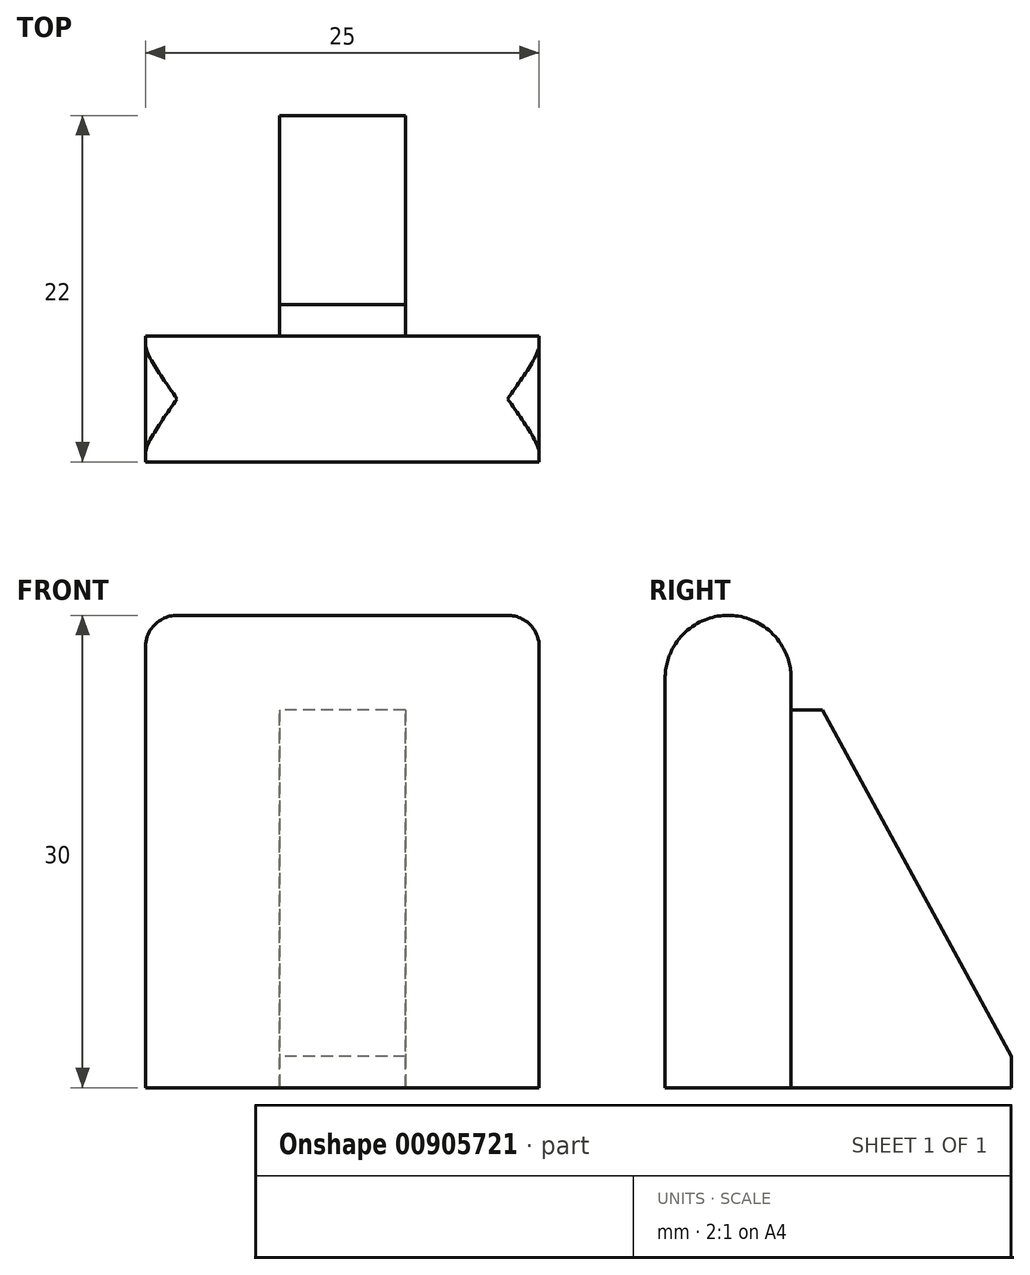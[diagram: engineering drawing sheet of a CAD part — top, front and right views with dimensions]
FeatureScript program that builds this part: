
annotation { "Feature Type Name" : "Feature", "Feature Type Description" : "" }
export const myFeature = defineFeature(function(context is Context, id is Id, definition is map)
    precondition{}
    {
        {
            var Q0;
            Q0=qCreatedBy(makeId("Right.planeOp"),FACE);
            var sketch = newSketch(context, id + "F0", { "sketchPlane" : qUnion([Q0])});
            skLineSegment(sketch, "E0.bottom", {"start": v(0, 0) * mm, "end": v(8, 0) * mm});
            skLineSegment(sketch, "E0.top", {"start": v(0, 26) * mm, "end": v(8, 26) * mm});
            skLineSegment(sketch, "E0.left", {"start": v(0, 0) * mm, "end": v(0, 26) * mm});
            skLineSegment(sketch, "E0.right", {"start": v(8, 0) * mm, "end": v(8, 26) * mm});
            skArc(sketch, "E1", {"start": v(0, 26) * mm, "mid": v(4, 30) * mm, "end": v(8, 26) * mm});
            skSolve(sketch);
        }
        {
            var Q0;
            Q0=makeQuery(id+"F0.imprint","IMPRINT",FACE,{"disambiguationData":[TD([[makeQuery(id+"F0.imprint","IMPRINT",EDGE,{"derivedFrom":sQuery(id+"F0.wireOp",EDGE,"E0.bottom")}),1.0]])]});
            var Q1;
            Q1=makeQuery(id+"F0.imprint","IMPRINT",FACE,{"disambiguationData":[TD([[makeQuery(id+"F0.imprint","IMPRINT",EDGE,{"derivedFrom":sQuery(id+"F0.wireOp",EDGE,"E0.top")}),1.0]])]});
            extrude(context, id + "F1", {"entities" : qUnion([Q0, Q1]), "endBound" : BoundingType.SYMMETRIC, "depth" : 25 * mm, "offsetDistance" : 25 * mm});
        }
        {
            var Q0;
            Q0=qCreatedBy(makeId("Right.planeOp"),FACE);
            var sketch = newSketch(context, id + "F2", { "sketchPlane" : qUnion([Q0])});
            skLineSegment(sketch, "E2.0.0", {"start": v(8, 0) * mm, "end": v(8, 26) * mm});
            skLineSegment(sketch, "E2.0.2", {"start": v(8, 26) * mm, "end": v(8, 0) * mm});
            skLineSegment(sketch, "E3", {"start": v(8, 24) * mm, "end": v(10, 24) * mm});
            skLineSegment(sketch, "E4", {"start": v(10, 24) * mm, "end": v(22, 2) * mm});
            skLineSegment(sketch, "E5", {"start": v(22, 2) * mm, "end": v(22, 0) * mm});
            skLineSegment(sketch, "E6", {"start": v(22, 0) * mm, "end": v(8, 0) * mm});
            skLineSegment(sketch, "E7.0.0", {"start": v(0, 0) * mm, "end": v(8, 0) * mm});
            skLineSegment(sketch, "E7.0.2", {"start": v(8, 0) * mm, "end": v(0, 0) * mm});
            skSolve(sketch);
        }
        {
            var Q0;
            Q0 = qSketchRegion(id + "F2", true);
            extrude(context, id + "F3", {"entities" : qUnion([Q0]), "operationType" : NewBodyOperationType.ADD, "endBound" : BoundingType.SYMMETRIC, "depth" : 8 * mm, "offsetDistance" : 25 * mm});
        }
        {
            var Q0;
            Q0=qCreatedBy(makeId("Front.planeOp"),FACE);
            var sketch = newSketch(context, id + "F4", { "sketchPlane" : qUnion([Q0])});
            skLineSegment(sketch, "E8.0.0", {"start": v(-12.5, 26) * mm, "end": v(-12.5, 0) * mm});
            skLineSegment(sketch, "E8.0.1", {"start": v(-12.5, 0) * mm, "end": v(12.5, 0) * mm});
            skLineSegment(sketch, "E8.0.2", {"start": v(12.5, 0) * mm, "end": v(12.5, 26) * mm});
            skLineSegment(sketch, "E8.0.3", {"start": v(12.5, 26) * mm, "end": v(-12.5, 26) * mm});
            skLineSegment(sketch, "E9", {"start": v(-12.5, 30) * mm, "end": v(-10.5, 30) * mm});
            skLineSegment(sketch, "E10.0.2", {"start": v(-12.5, 0) * mm, "end": v(-12.5, 26) * mm});
            skLineSegment(sketch, "E10.0.3", {"start": v(-12.5, 28) * mm, "end": v(-12.5, 30) * mm});
            skLineSegment(sketch, "E11.0.1", {"start": v(12.5, 28) * mm, "end": v(12.5, 30) * mm});
            skLineSegment(sketch, "E11.0.2", {"start": v(12.5, 26) * mm, "end": v(12.5, 0) * mm});
            skArc(sketch, "E12", {"start": v(-12.5, 28) * mm, "mid": v(-11.91, 29.41) * mm, "end": v(-10.5, 30) * mm});
            skArc(sketch, "E13", {"start": v(10.5, 30) * mm, "mid": v(11.91, 29.41) * mm, "end": v(12.5, 28) * mm});
            skLineSegment(sketch, "E14.trimOffspring", {"start": v(10.5, 30) * mm, "end": v(12.5, 30) * mm});
            skSolve(sketch);
        }
        {
            var Q0;
            Q0=makeQuery(id+"F4.imprint","IMPRINT",FACE,{"disambiguationData":[TD([[makeQuery(id+"F4.imprint","IMPRINT",EDGE,{"derivedFrom":sQuery(id+"F4.wireOp",EDGE,"E9")}),-1.0]])]});
            var Q1;
            Q1=makeQuery(id+"F4.imprint","IMPRINT",FACE,{"disambiguationData":[TD([[makeQuery(id+"F4.imprint","IMPRINT",EDGE,{"derivedFrom":sQuery(id+"F4.wireOp",EDGE,"E11.0.1")}),1.0]])]});
            extrude(context, id + "F5", {"entities" : qUnion([Q0, Q1]), "operationType" : NewBodyOperationType.REMOVE, "oppositeDirection" : true, "depth" : 25 * mm, "offsetDistance" : 25 * mm});
        }
    });
